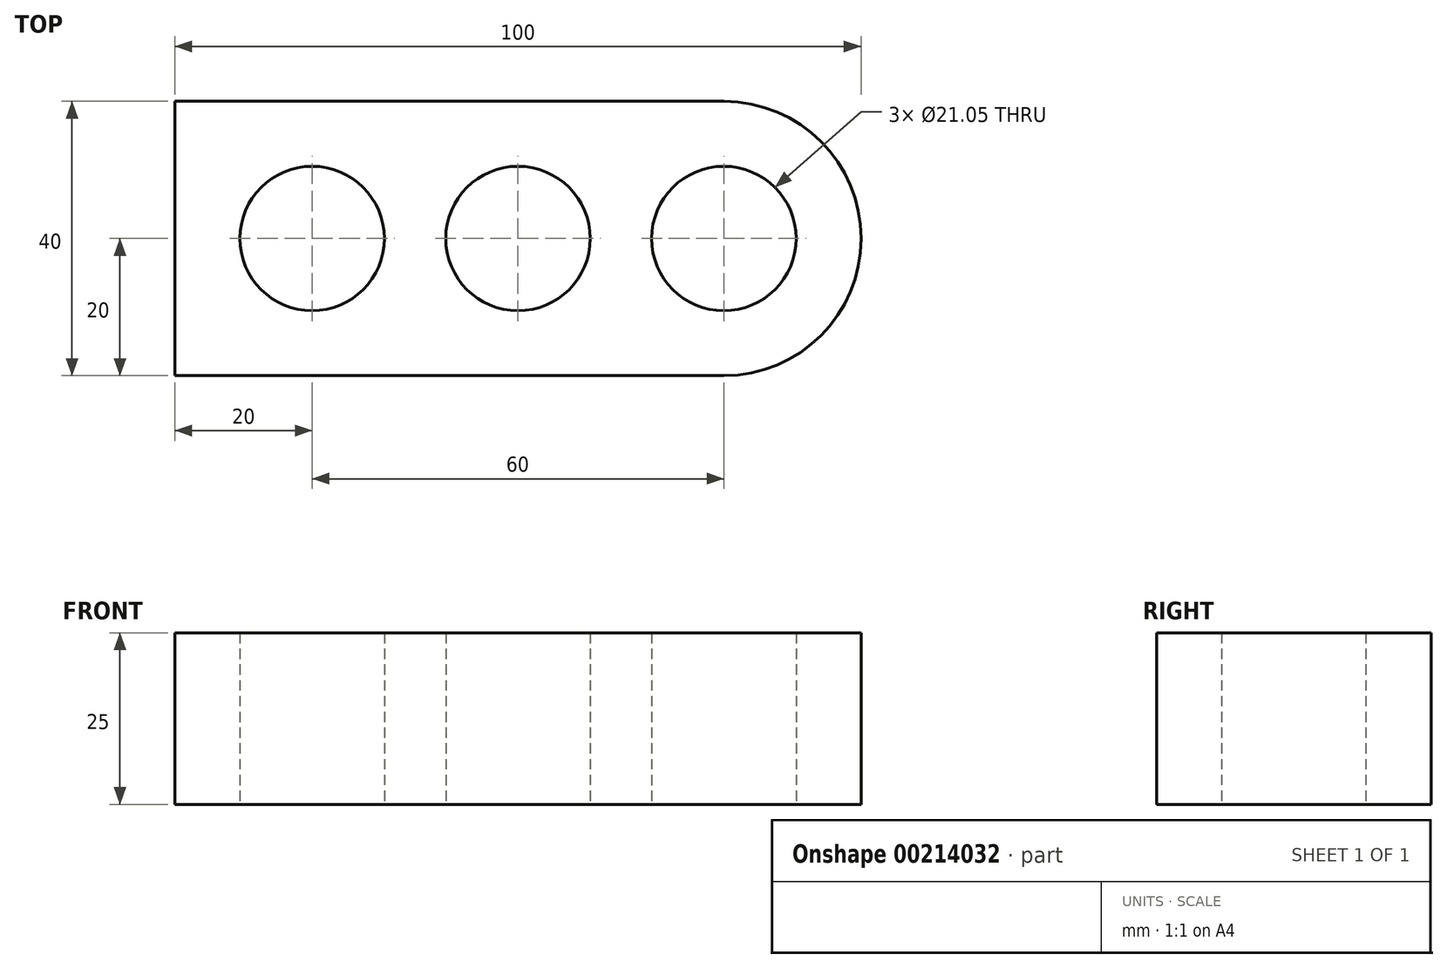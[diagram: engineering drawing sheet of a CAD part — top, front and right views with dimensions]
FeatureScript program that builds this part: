
annotation { "Feature Type Name" : "Feature", "Feature Type Description" : "" }
export const myFeature = defineFeature(function(context is Context, id is Id, definition is map)
    precondition{}
    {
        {
            var Q0;
            Q0=qCreatedBy(makeId("Top.planeOp"),FACE);
            var sketch = newSketch(context, id + "F0", { "sketchPlane" : qUnion([Q0])});
            skLineSegment(sketch, "E0.bottom", {"start": v(30, 20) * mm, "end": v(-50, 20) * mm});
            skLineSegment(sketch, "E0.top", {"start": v(30, -20) * mm, "end": v(-50, -20) * mm});
            skLineSegment(sketch, "E0.right", {"start": v(-50, 20) * mm, "end": v(-50, -20) * mm});
            skPoint(sketch, "E0.middle", {"position": v(0, 0) * mm});
            skLineSegment(sketch, "E1", {"start": v(30, -20) * mm, "end": v(30, 20) * mm});
            skArc(sketch, "E2", {"start": v(30, -20) * mm, "mid": v(50, 0) * mm, "end": v(30, 20) * mm});
            skPoint(sketch, "E3.orphan", {"position": v(50, 20) * mm});
            skPoint(sketch, "E0.left.end.orphan", {"position": v(50, -20) * mm});
            skSolve(sketch);
        }
        {
            var Q0;
            Q0 = qSketchRegion(id + "F0", true);
            extrude(context, id + "F1", {"entities" : qUnion([Q0]), "depth" : 25 * mm});
        }
        {
            var Q0;
            Q0=makeQuery(id+"F1.opExtrude","CAP_FACE",FACE,{"disambiguationData":[OSD([sQuery(id+"F0.wireOp",EDGE,"E0.bottom"),sQuery(id+"F0.wireOp",EDGE,"E0.top"),sQuery(id+"F0.wireOp",EDGE,"E0.right"),sQuery(id+"F0.wireOp",EDGE,"E2")])],"isStart":true});
            var sketch = newSketch(context, id + "F2", { "sketchPlane" : qUnion([Q0])});
            skLineSegment(sketch, "E4", {"start": v(-50, 0) * mm, "end": v(66.54, 0) * mm, "construction": true});
            skPoint(sketch, "E4.endSnap0", {"position": v(50, 0) * mm});
            skCircle(sketch, "E5", {"center": v(30, 0) * mm, "radius": 10.53 * mm});
            skCircle(sketch, "E6", {"center": v(0, 0) * mm, "radius": 10.53 * mm});
            skCircle(sketch, "E7", {"center": v(-30, 0) * mm, "radius": 10.53 * mm});
            skSolve(sketch);
        }
        {
            var Q0;
            Q0 = qSketchRegion(id + "F2", true);
            extrude(context, id + "F3", {"entities" : qUnion([Q0]), "operationType" : NewBodyOperationType.REMOVE, "endBound" : BoundingType.UP_TO_NEXT, "oppositeDirection" : true, "depth" : 25 * mm});
        }
    });
